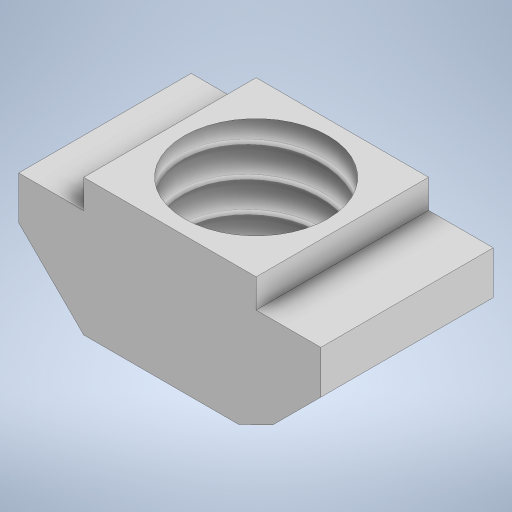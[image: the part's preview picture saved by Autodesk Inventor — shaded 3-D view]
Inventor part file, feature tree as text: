
AUTODESK INVENTOR PART (.ipt)
format: ipt  version: 2023.5 (Build 275446000, 446)  size: 253,440 bytes
history: native  units: in
note: dims shown in document units (in); Inventor stores cm internally (conversion verified against a paired STEP export)
features: sketch x2, extrude x1, hole x1, thread x1
ambient origin geometry x8: Origin, YZ Plane, XZ Plane, XY Plane, X Axis, Y Axis, Z Axis, Center Point
bodies: Solid1 (feature_tree)
feature tree (5):
  extrude  "Extrusion1"  Depth=0.2362in TaperAngle=0.0deg
  hole  "Hole2"  [1 undecoded]
  thread  "Thread2"  [1 undecoded]
  sketch  "Sketch1"  dims[d0=0.0394in d1=0.2362in d2=0.0886in d3=0.0591in d4=0.093in d5=135.0deg d6=0.089in d7=0.2362in d8=0.0in]
  sketch  "Sketch5"  dims[d19=0.1969in d20=0.1969in d21=0.75in d22=0.375in d23=0.25in d24=0.5635in d25=1.0in d26=0.8108in d27=0.187in d28=0.0in]
note: 2 required parameter values undecoded (feature->parameter linkage not recoverable at this tier; creation-order binding heuristic only, values carry confidence <= 0.55)
